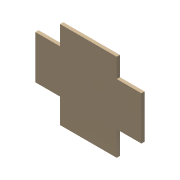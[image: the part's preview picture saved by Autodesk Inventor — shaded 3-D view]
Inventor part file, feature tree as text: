
AUTODESK INVENTOR PART (.ipt)
format: ipt  version: 2015 SP1 (Build 190203100, 203)  size: 80,896 bytes
history: native  units: mm
features: other x1, extrude x1, sketch x1
ambient origin geometry x8: Origin, YZ Plane, XZ Plane, XY Plane, X Axis, Y Axis, Z Axis, Center Point
bodies: Body1 (feature_tree)
feature tree (3):
  other  "Твердое тело1"
  extrude  "Выдавливание1"  Depth=13.54mm
  sketch  "Эскиз1"
